# Revit family: O5UM-NRG
name_source: partatom
category: Mechanical Equipment
units: mm (PartAtom-declared; Revit-internal decimal feet)

## family parameters
Always vertical = Yes
Cut with Voids When Loaded = No
OmniClass Number = 23.40.40.11.17
OmniClass Title = Refrigerated Cases
Part Type = Normal
Room Calculation Point = No
Round Connector Dimension = Use Radius
Shared = No
Work Plane-Based = Yes

## types (5) — shared parameters
11" BF = Yes
ANTI SWEAT APPARENT LOAD = 0 VA
ANTI SWEAT HEATER AMPS = 0 A
ANTI SWEAT HEATER WATTAGE = 0 W
Application Discipline = Dairy/Deli/Produce
BASE HEIGHT = 5 1/8"
BTU PER FOOT CONVENTIONAL = 1091
BTU PER FOOT PARALLEL = 1000
BTUH Conventional = 1143
BTUH Parallel = 1000
CERTIFICATIONS = NSF 7, UL471, CSA
COIL REFRIGERATION CHARGE = 0.00 lb
CONTROL TYPE = T-STAT
DATE = 08/01/12
DEDICATED CIRCUIT = YES
DEFROST AMPS = 0 A
DEFROST PHASE = 1
DEFROST TIME AND DURATION = 2 @ 60 MIN
DEFROST WATTAGE = 0 W
DIEBOARD HEIGHT = 0"
DISCHARGE AIR TEMPERATURE = 31 °F
DRAIN LINE CONNECTION = Drain Connection
DRAIN LINE DIAMETER = 2"
DRAIN LINE RADIUS = 1"
DRAIN PIPE TYPE = PVC
DRIP PAN PLUMB TYPE = HARD
Default Elevation = 48"
Defrosts Per Day = 6
Description = MULTI DECK MERCHANDISER
Discharge Air (°F) = 31 °F
Discharge Air Velocity (FPM) = 180 FPM
ELECTRIC DEFROST = No
ELECTRICAL DEFROST VOLTAGE = 0 V
EVAPORATOR TEMPERATURE = 28 °F
Evaporator (°F) = 28 °F
FAN CONNECTOR DESCRIPTION = FAN AND ANTI SWEAT CONNECTOR
FAN NUMBER OF POLES = 1
FAN TYPE = ECM
Front Sill Height = All
GROUND FAULT PROTECTION = NO
HEIGHT = 66 1/8"
HOT GAS DEFROST = No
High Power (Cornice) Amps = 0 A
ISOLATED GROUND REQUIRED = NO
Keynote = DAIRY/DELI/PRODUCE
LED LIGHTING AMPS PER ROW = 0 A
LIGHT TYPE = T8 FLUORESCENT
LIGHTING CONNECTION DESCRIPTION = LIGHTING CONNECTOR
LIGHTING NUMBER OF POLES = 1
LIQUID LINE CONNECTION = LIQUID LINE CONNECTION
LIQUID LINE DIAMETER = 0"
LIQUID LINE RADIUS = 0"
Manufacturer = HILL PHOENIX
NUMBER OF WIRES = 3
PHASE = 1
POWER FACTOR = 1
PRESSURE REGULATOR = 0.00 psi
RECEPTICAL MOUNTING HEIGHT ABOVE FLOOR = 19 3/4"
REF PLANE FRONT BACK = 21 5/8"
REVERSE AIR DEFROST = No
SET BACK MODE FOR ENERGY CONSERVATION = NO
SHELVE 1 = Yes
SIZE OF COLD WATER HOOK UP = 0"
SIZE OF HOT WATER HOOK-UP = 0"
SUCTION LINE CONNECTION = SUCTION LINE CONNECTION
SUCTION LINE DIAMETER = 1"
SUCTION LINE RADIUS = 0"
Standard Power Amps = 0 A
Superheat Set Point @ Bulb (°F) = 6-8
T8 LIGHT OR LED LIGHT = Yes
TIME OFF DEFROST = Yes
TOEKICK HEIGHT = 5 1/2"
TOEKICK INSET = 1 1/2"
Timed-Off Defrost Fail-Safe (Min) = 30
Timed-Off Defrost Termination Temp = 42 °F
URL = http://www.hillphoenix.com
VOLTAGE = 120 V
WATER LINE MOUNTING HEIGHT ABOVE FLOOR = 0"
WEIGHT = 0.00 lb
WIDTH = 43 1/4"
zero-valued in all types: CORNICE AND NOSE LIGHT ROWS

## per-type parameters (varying)
- O5UM-NRG-12': 5" BF=Yes; BTU ADD FOR LIGHTS=3312; BTU ADD PER SHELF PER FOOT=92; CONVENTIONAL EVAPORATOR LOAD=16404; DRAIN PIPE LENGTH=0"; FAN AMPS=1 A; FAN AND ANTI SWEAT HEATER APPARENT LOAD=72 VA; FAN APPARENT LOAD=72 VA; FAN QUANTITY=3; FAN WATTAGE=42 W; High Efficiency Amps=1 A; High Efficiency Watts=42 W; High Power (Cornice) Watts=45 W; LED LIGHTING AMPS=1 A; LED LIGHTING BTU ADD PER ROW=36; LED LIGHTING WATTAGE=108 W; LEGEND NUMBER=O5UM-NRG-12'; LENGTH=144"; LENGTH FOR BTU=12; LIGHT AMPS=2 A; LIGHTING APPARENT LOAD=252 VA; LIGHTING WATTAGE=252 VA; Light Length=4'; Lights Per Row=3; Model=O5UM-NRG-12'; Number of Fans=3; PARALLEL EVAPORATOR LOAD=15312; REF PIPE LENGTH=28 5/8"; REF PLANE LEFT RIGHT=72"; SHELF LIGHT ROWS=3; SHELVE 2=Yes; SHELVE 3=Yes; SHELVE LENGTH=48"; Standard Power Watts=18 W; T8 LIGHTING AMPS=2 A; T8 LIGHTING AMPS PER ROW=1 A; T8 LIGHTING BTU ADD PER ROW=92; T8 LIGHTING WATTAGE=252 W; TOTAL APPARENT FAN-LIGHT AND A/S LOAD=294 VA; TOTAL CASE AMPS=3 A; TOTAL CASE WATTAGE=294 W
- O5UM-NRG-08': 5" BF=Yes; BTU ADD FOR LIGHTS=1472; BTU ADD PER SHELF PER FOOT=92; CONVENTIONAL EVAPORATOR LOAD=10200; DRAIN PIPE LENGTH=0"; FAN AMPS=0 A; FAN AND ANTI SWEAT HEATER APPARENT LOAD=48 VA; FAN APPARENT LOAD=48 VA; FAN QUANTITY=2; FAN WATTAGE=28 W; High Efficiency Amps=0 A; High Efficiency Watts=28 W; High Power (Cornice) Watts=30 W; LED LIGHTING AMPS=0 A; LED LIGHTING BTU ADD PER ROW=36; LED LIGHTING WATTAGE=48 W; LEGEND NUMBER=O5UM-NRG-8'; LENGTH=96"; LENGTH FOR BTU=8; LIGHT AMPS=1 A; LIGHTING APPARENT LOAD=113 VA; LIGHTING WATTAGE=113 VA; Light Length=4'; Lights Per Row=2; Model=O5UM-NRG-8'; Number of Fans=2; PARALLEL EVAPORATOR LOAD=9472; REF PIPE LENGTH=28 5/8"; REF PLANE LEFT RIGHT=48"; SHELF LIGHT ROWS=2; SHELVE 2=No; SHELVE 3=Yes; SHELVE LENGTH=48"; Standard Power Watts=12 W; T8 LIGHTING AMPS=1 A; T8 LIGHTING AMPS PER ROW=0 A; T8 LIGHTING BTU ADD PER ROW=92; T8 LIGHTING WATTAGE=113 W; TOTAL APPARENT FAN-LIGHT AND A/S LOAD=141 VA; TOTAL CASE AMPS=1 A; TOTAL CASE WATTAGE=141 W
- O5UM-NRG-06': 5" BF=No; BTU ADD FOR LIGHTS=828; BTU ADD PER SHELF PER FOOT=69; CONVENTIONAL EVAPORATOR LOAD=7374; DRAIN PIPE LENGTH=0"; FAN AMPS=0 A; FAN AND ANTI SWEAT HEATER APPARENT LOAD=48 VA; FAN APPARENT LOAD=48 VA; FAN QUANTITY=2; FAN WATTAGE=28 W; High Efficiency Amps=40 A; High Efficiency Watts=28 W; High Power (Cornice) Watts=24 W; LED LIGHTING AMPS=0 A; LED LIGHTING BTU ADD PER ROW=27; LED LIGHTING WATTAGE=34 W; LEGEND NUMBER=O5UM-NRG-6'; LENGTH=72"; LENGTH FOR BTU=6; LIGHT AMPS=1 A; LIGHTING APPARENT LOAD=89 VA; LIGHTING WATTAGE=89 VA; Light Length=3'; Lights Per Row=2; Model=O5UM-NRG-6'; Number of Fans=2; PARALLEL EVAPORATOR LOAD=6828; REF PIPE LENGTH=28 5/8"; REF PLANE LEFT RIGHT=36"; SHELF LIGHT ROWS=2; SHELVE 2=No; SHELVE 3=Yes; SHELVE LENGTH=36"; Standard Power Watts=9 W; T8 LIGHTING AMPS=1 A; T8 LIGHTING AMPS PER ROW=0 A; T8 LIGHTING BTU ADD PER ROW=69; T8 LIGHTING WATTAGE=89 W; TOTAL APPARENT FAN-LIGHT AND A/S LOAD=117 VA; TOTAL CASE AMPS=1 A; TOTAL CASE WATTAGE=117 W
- O5UM-NRG-04': 5" BF=No; BTU ADD FOR LIGHTS=368; BTU ADD PER SHELF PER FOOT=92; CONVENTIONAL EVAPORATOR LOAD=4732; DRAIN PIPE LENGTH=12"; FAN AMPS=0 A; FAN AND ANTI SWEAT HEATER APPARENT LOAD=24 VA; FAN APPARENT LOAD=24 VA; FAN QUANTITY=1; FAN WATTAGE=14 W; High Efficiency Amps=0 A; High Efficiency Watts=14 W; High Power (Cornice) Watts=22 W; LED LIGHTING AMPS=0 A; LED LIGHTING BTU ADD PER ROW=36; LED LIGHTING WATTAGE=12 W; LEGEND NUMBER=O5UM-NRG; LENGTH=48"; LENGTH FOR BTU=4; LIGHT AMPS=0 A; LIGHTING APPARENT LOAD=28 VA; LIGHTING WATTAGE=28 VA; Light Length=4'; Lights Per Row=1; Model=O5UM-NRG; Number of Fans=1; PARALLEL EVAPORATOR LOAD=4368; REF PIPE LENGTH=22 3/4"; REF PLANE LEFT RIGHT=24"; SHELF LIGHT ROWS=1; SHELVE 2=No; SHELVE 3=No; SHELVE LENGTH=48"; Standard Power Watts=6 W; T8 LIGHTING AMPS=0 A; T8 LIGHTING AMPS PER ROW=0 A; T8 LIGHTING BTU ADD PER ROW=92; T8 LIGHTING WATTAGE=28 W; TOTAL APPARENT FAN-LIGHT AND A/S LOAD=42 VA; TOTAL CASE AMPS=0 A; TOTAL CASE WATTAGE=42 W
- O5UM-NRG-10': 5" BF=Yes; BTU ADD FOR LIGHTS=2760; BTU ADD PER SHELF PER FOOT=92; CONVENTIONAL EVAPORATOR LOAD=13670; DRAIN PIPE LENGTH=0"; FAN AMPS=1 A; FAN AND ANTI SWEAT HEATER APPARENT LOAD=72 VA; FAN APPARENT LOAD=72 VA; FAN QUANTITY=3; FAN WATTAGE=42 W; High Efficiency Amps=1 A; High Efficiency Watts=42 W; High Power (Cornice) Watts=45 W; LED LIGHTING AMPS=1 A; LED LIGHTING BTU ADD PER ROW=36; LED LIGHTING WATTAGE=108 W; LEGEND NUMBER=O5UM-NRG-12'; LENGTH=120"; LENGTH FOR BTU=10; LIGHT AMPS=2 A; LIGHTING APPARENT LOAD=252 VA; LIGHTING WATTAGE=252 VA; Light Length=4'; Lights Per Row=3; Model=O5UM-NRG-12'; Number of Fans=3; PARALLEL EVAPORATOR LOAD=12760; REF PIPE LENGTH=28 5/8"; REF PLANE LEFT RIGHT=60"; SHELF LIGHT ROWS=3; SHELVE 2=Yes; SHELVE 3=Yes; SHELVE LENGTH=48"; Standard Power Watts=18 W; T8 LIGHTING AMPS=2 A; T8 LIGHTING AMPS PER ROW=1 A; T8 LIGHTING BTU ADD PER ROW=92; T8 LIGHTING WATTAGE=252 W; TOTAL APPARENT FAN-LIGHT AND A/S LOAD=294 VA; TOTAL CASE AMPS=3 A; TOTAL CASE WATTAGE=294 W

## geometry (parser evidence)
native form markers: Blend x2, Sweep x1
no freeform markers — native parametric forms only
